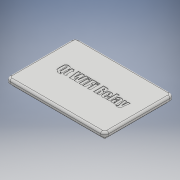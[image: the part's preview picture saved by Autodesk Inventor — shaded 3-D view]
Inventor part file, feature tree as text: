
AUTODESK INVENTOR PART (.ipt)
format: ipt  version: 2018 (Build 220112000, 112)  size: 379,904 bytes
history: native  units: mm
features: sketch x4, extrude x3, chamfer x2, fillet x2, emboss x1
ambient origin geometry x8: Origin, YZ Plane, XZ Plane, XY Plane, X Axis, Y Axis, Z Axis, Center Point
bodies: Solid1 (feature_tree)
feature tree (12):
  extrude  "Extrusion1"  Depth=31.5mm
  extrude  "Extrusion2"  Depth=1.4mm
  extrude  "Extrusion3"  Depth=3.0mm
  chamfer  "Chamfer1"  Distance=2.0mm
  chamfer  "Chamfer2"  Distance=0.5mm Angle=45.0deg
  fillet  "Fillet1"  Radius=2.0mm
  fillet  "Fillet2"  Radius=1.0mm
  emboss  "Emboss1"
  sketch  "Sketch1"  dims[d0=46.0mm d1=31.5mm]
  sketch  "Sketch2"  dims[d2=2.0mm d3=0.0mm d4=1.4mm]
  sketch  "Sketch3"  dims[d5=2.0mm d6=0.0mm d7=3.0mm d8=2.0mm d9=0.0mm d10=0.5mm d11=2.0mm d12=45.0deg]
  sketch  "Sketch4"  dims[d13=0.5mm d14=2.0mm d15=45.0deg d16=2.0mm d17=1.0mm d18=0.2mm d19=0.0mm]
